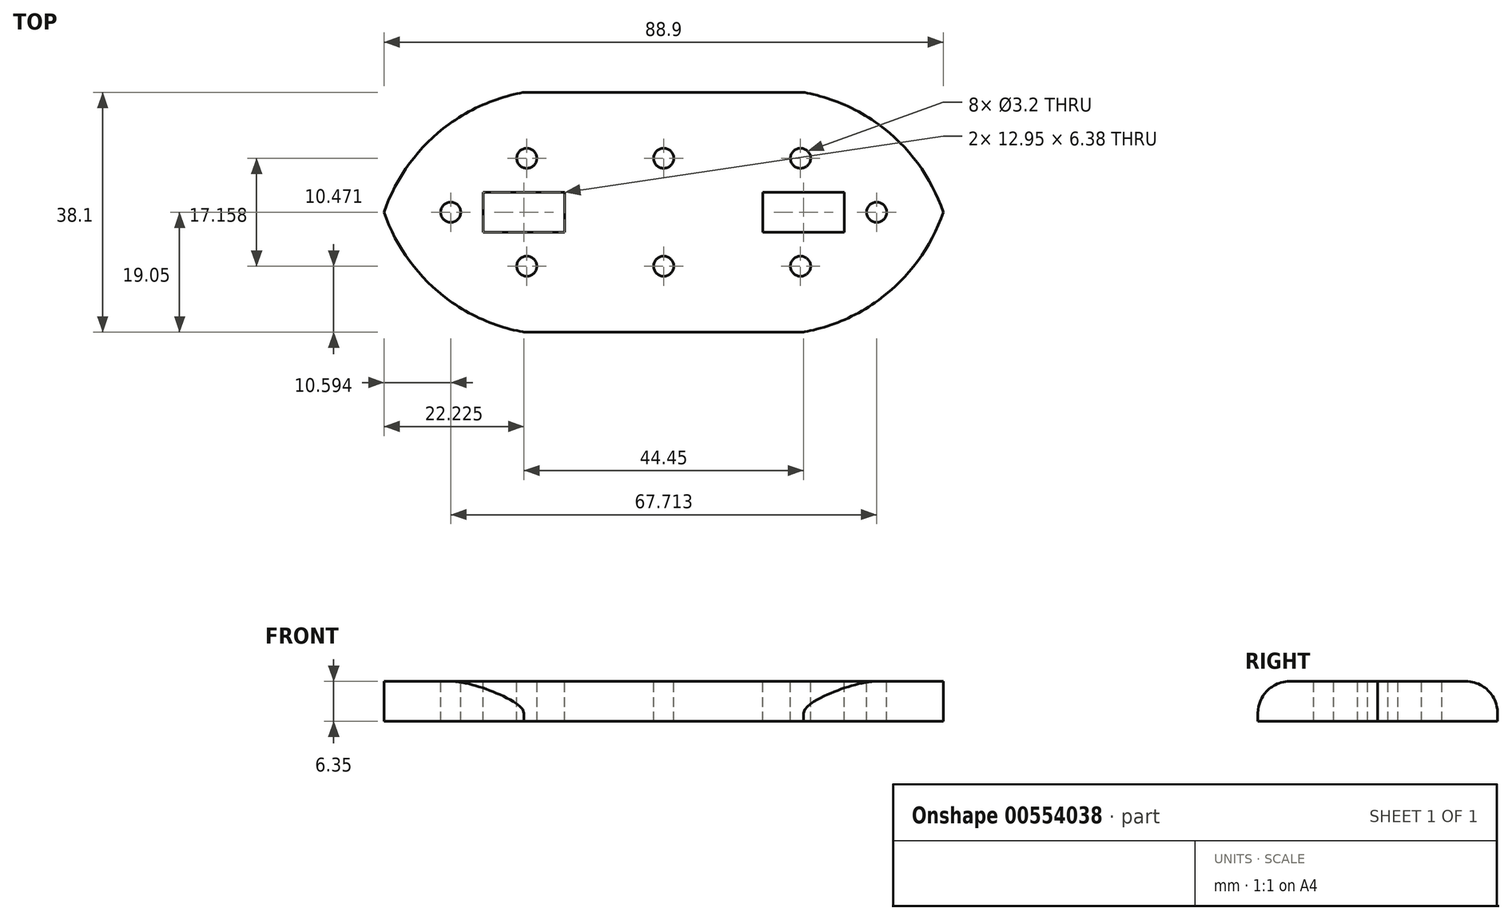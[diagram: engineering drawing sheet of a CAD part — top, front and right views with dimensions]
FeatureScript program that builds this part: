
annotation { "Feature Type Name" : "Feature", "Feature Type Description" : "" }
export const myFeature = defineFeature(function(context is Context, id is Id, definition is map)
    precondition{}
    {
        {
            var Q0;
            Q0=qCreatedBy(makeId("Top.planeOp"),FACE);
            var sketch = newSketch(context, id + "F0", { "sketchPlane" : qUnion([Q0])});
            skLineSegment(sketch, "E0.bottom", {"start": v(44.45, 19.05) * mm, "end": v(-44.45, 19.05) * mm});
            skLineSegment(sketch, "E0.top", {"start": v(44.45, -19.05) * mm, "end": v(-44.45, -19.05) * mm});
            skLineSegment(sketch, "E0.left", {"start": v(44.45, 19.05) * mm, "end": v(44.45, -19.05) * mm});
            skLineSegment(sketch, "E0.right", {"start": v(-44.45, 19.05) * mm, "end": v(-44.45, -19.05) * mm});
            skPoint(sketch, "E0.middle", {"position": v(0, 0) * mm});
            skSolve(sketch);
        }
        {
            var Q0;
            Q0 = qSketchRegion(id + "F0", true);
            extrude(context, id + "F1", {"entities" : qUnion([Q0]), "depth" : 6.35 * mm, "offsetDistance" : 25.4 * mm});
        }
        {
            var Q0;
            Q0=makeQuery(id+"F1.opExtrude","CAP_FACE",FACE,{"disambiguationData":[OSD([sQuery(id+"F0.wireOp",EDGE,"E0.bottom"),sQuery(id+"F0.wireOp",EDGE,"E0.top"),sQuery(id+"F0.wireOp",EDGE,"E0.left"),sQuery(id+"F0.wireOp",EDGE,"E0.right")])],"isStart":false});
            var sketch = newSketch(context, id + "F2", { "sketchPlane" : qUnion([Q0])});
            skLineSegment(sketch, "E1", {"start": v(0, 19.05) * mm, "end": v(44.45, 19.05) * mm, "construction": true});
            skLineSegment(sketch, "E2", {"start": v(-44.45, 19.05) * mm, "end": v(0, 19.05) * mm, "construction": true});
            skLineSegment(sketch, "E3", {"start": v(0, 19.05) * mm, "end": v(0, -5.07) * mm, "construction": true});
            skArc(sketch, "E4", {"start": v(-22.23, 19.05) * mm, "mid": v(-35.93, 12.55) * mm, "end": v(-44.45, 0) * mm});
            skArc(sketch, "E5.MirrorCS", {"start": v(22.23, 19.05) * mm, "mid": v(35.93, 12.55) * mm, "end": v(44.45, 0) * mm});
            skLineSegment(sketch, "E6", {"start": v(0, 0) * mm, "end": v(25.9, 0) * mm, "construction": true});
            skArc(sketch, "E7.MirrorCS", {"start": v(22.23, -19.05) * mm, "mid": v(35.93, -12.55) * mm, "end": v(44.45, 0) * mm});
            skArc(sketch, "E8.MirrorCS", {"start": v(-22.23, -19.05) * mm, "mid": v(-35.93, -12.55) * mm, "end": v(-44.45, 0) * mm});
            skLineSegment(sketch, "E9", {"start": v(-22.23, -19.05) * mm, "end": v(-55.77, -34.2) * mm, "construction": true});
            skLineSegment(sketch, "E10", {"start": v(-55.77, -34.2) * mm, "end": v(-22.23, -19.05) * mm});
            skLineSegment(sketch, "E11", {"start": v(-55.77, -34.2) * mm, "end": v(-59.27, 33.28) * mm});
            skLineSegment(sketch, "E12", {"start": v(-59.27, 33.28) * mm, "end": v(-22.22, 19.05) * mm});
            skLineSegment(sketch, "E13", {"start": v(22.23, 19.05) * mm, "end": v(83.05, 33.83) * mm});
            skLineSegment(sketch, "E14", {"start": v(83.05, 33.83) * mm, "end": v(77.7, -26.82) * mm});
            skLineSegment(sketch, "E15", {"start": v(77.7, -26.82) * mm, "end": v(22.23, -19.05) * mm});
            skSolve(sketch);
        }
        {
            var Q0;
            Q0 = qSketchRegion(id + "F2", true);
            extrude(context, id + "F3", {"entities" : qUnion([Q0]), "operationType" : NewBodyOperationType.REMOVE, "oppositeDirection" : true, "depth" : 25.4 * mm, "offsetDistance" : 25.4 * mm});
        }
        {
            var Q0;
            Q0=makeQuery(id+"F1.opExtrude","CAP_FACE",FACE,{"disambiguationData":[OSD([sQuery(id+"F0.wireOp",EDGE,"E0.bottom"),sQuery(id+"F0.wireOp",EDGE,"E0.top"),sQuery(id+"F0.wireOp",EDGE,"E0.left"),sQuery(id+"F0.wireOp",EDGE,"E0.right")])],"isStart":false});
            var sketch = newSketch(context, id + "F4", { "sketchPlane" : qUnion([Q0])});
            skLineSegment(sketch, "E16", {"start": v(0, 19.05) * mm, "end": v(0, -19.05) * mm, "construction": true});
            skLineSegment(sketch, "E17", {"start": v(-22.23, 19.05) * mm, "end": v(-22.22, -19.05) * mm, "construction": true});
            skLineSegment(sketch, "E18", {"start": v(22.22, 19.05) * mm, "end": v(22.22, -19.05) * mm, "construction": true});
            skLineSegment(sketch, "E19.bottom", {"start": v(-15.75, 3.19) * mm, "end": v(-28.7, 3.19) * mm});
            skLineSegment(sketch, "E19.top", {"start": v(-15.75, -3.19) * mm, "end": v(-28.7, -3.19) * mm});
            skLineSegment(sketch, "E19.left", {"start": v(-15.75, 3.19) * mm, "end": v(-15.75, -3.19) * mm});
            skLineSegment(sketch, "E19.right", {"start": v(-28.7, 3.19) * mm, "end": v(-28.7, -3.19) * mm});
            skPoint(sketch, "E19.middle", {"position": v(-22.22, 0) * mm});
            skLineSegment(sketch, "E20.MirrorCS", {"start": v(15.75, 3.19) * mm, "end": v(28.7, 3.19) * mm});
            skLineSegment(sketch, "E21.MirrorCS", {"start": v(15.75, -3.19) * mm, "end": v(28.7, -3.19) * mm});
            skLineSegment(sketch, "E22.MirrorCS", {"start": v(15.75, 3.19) * mm, "end": v(15.75, -3.19) * mm});
            skLineSegment(sketch, "E23.MirrorCS", {"start": v(28.7, 3.19) * mm, "end": v(28.7, -3.19) * mm});
            skSolve(sketch);
        }
        {
            var Q0;
            Q0 = qSketchRegion(id + "F4", true);
            extrude(context, id + "F5", {"entities" : qUnion([Q0]), "operationType" : NewBodyOperationType.REMOVE, "oppositeDirection" : true, "depth" : 25.4 * mm, "offsetDistance" : 25.4 * mm});
        }
        {
            var Q0;
            Q0=makeQuery(id+"F3.boolean.opBoolean","COPY",EDGE,{"derivedFrom":makeQuery(id+"F3.opExtrude","CAP_EDGE",EDGE,{"disambiguationData":[OSD([sQuery(id+"F2.wireOp",EDGE,"E8.MirrorCS")])],"isStart":true})});
            var Q1;
            Q1=makeQuery(id+"F3.boolean.opBoolean","COPY",EDGE,{"derivedFrom":makeQuery(id+"F3.opExtrude","CAP_EDGE",EDGE,{"disambiguationData":[OSD([sQuery(id+"F2.wireOp",EDGE,"E4")])],"isStart":true})});
            var Q2;
            Q2=makeQuery(id+"F1.opExtrude","CAP_EDGE",EDGE,{"disambiguationData":[OSD([sQuery(id+"F0.wireOp",EDGE,"E0.bottom")])],"isStart":false});
            var Q3;
            Q3=makeQuery(id+"F1.opExtrude","CAP_EDGE",EDGE,{"disambiguationData":[OSD([sQuery(id+"F0.wireOp",EDGE,"E0.top")])],"isStart":false});
            var Q4;
            Q4=makeQuery(id+"F3.boolean.opBoolean","COPY",EDGE,{"derivedFrom":makeQuery(id+"F3.opExtrude","CAP_EDGE",EDGE,{"disambiguationData":[OSD([sQuery(id+"F2.wireOp",EDGE,"E7.MirrorCS")])],"isStart":true})});
            var Q5;
            Q5=makeQuery(id+"F3.boolean.opBoolean","COPY",EDGE,{"derivedFrom":makeQuery(id+"F3.opExtrude","CAP_EDGE",EDGE,{"disambiguationData":[OSD([sQuery(id+"F2.wireOp",EDGE,"E5.MirrorCS")])],"isStart":true})});
            fillet(context, id + "F6", {"entities" : qUnion([Q0, Q1, Q2, Q3, Q4, Q5]), "tangentPropagation" : true, "radius" : 5.08 * mm, "defaultsChanged" : false, "vertexSettings" : [], "allowEdgeOverflow" : false});
        }
        {
            var Q0;
            Q0=makeQuery(id+"F1.opExtrude","CAP_FACE",FACE,{"disambiguationData":[OSD([sQuery(id+"F0.wireOp",EDGE,"E0.bottom"),sQuery(id+"F0.wireOp",EDGE,"E0.top"),sQuery(id+"F0.wireOp",EDGE,"E0.left"),sQuery(id+"F0.wireOp",EDGE,"E0.right")])],"isStart":false});
            var sketch = newSketch(context, id + "F7", { "sketchPlane" : qUnion([Q0])});
            skLineSegment(sketch, "E24", {"start": v(-21.75, 13.97) * mm, "end": v(-21.75, -13.97) * mm, "construction": true});
            skLineSegment(sketch, "E25", {"start": v(-39.01, 0) * mm, "end": v(39.01, 0) * mm, "construction": true});
            skLineSegment(sketch, "E26", {"start": v(0, 13.97) * mm, "end": v(0, -13.97) * mm, "construction": true});
            skLineSegment(sketch, "E27", {"start": v(21.75, 13.97) * mm, "end": v(21.75, -13.97) * mm, "construction": true});
            skLineSegment(sketch, "E28", {"start": v(-39.01, 0) * mm, "end": v(-28.7, 0) * mm, "construction": true});
            skLineSegment(sketch, "E29", {"start": v(28.7, 0) * mm, "end": v(39.01, 0) * mm, "construction": true});
            skLineSegment(sketch, "E30", {"start": v(-21.75, 13.97) * mm, "end": v(-21.75, 3.19) * mm, "construction": true});
            skLineSegment(sketch, "E31", {"start": v(-21.75, -13.97) * mm, "end": v(-21.75, -3.19) * mm, "construction": true});
            skLineSegment(sketch, "E32", {"start": v(21.75, -3.19) * mm, "end": v(21.75, -13.97) * mm, "construction": true});
            skLineSegment(sketch, "E33", {"start": v(21.75, 3.19) * mm, "end": v(21.75, 13.97) * mm, "construction": true});
            skCircle(sketch, "E34", {"center": v(-33.86, 0) * mm, "radius": 1.6 * mm});
            skCircle(sketch, "E35", {"center": v(-21.75, 8.58) * mm, "radius": 1.6 * mm});
            skCircle(sketch, "E36.MirrorC", {"center": v(33.86, 0) * mm, "radius": 1.6 * mm});
            skCircle(sketch, "E37.MirrorC", {"center": v(21.75, 8.58) * mm, "radius": 1.6 * mm});
            skLineSegment(sketch, "E38.MirrorCS", {"start": v(39.01, 0) * mm, "end": v(-39.01, 0) * mm, "construction": true});
            skCircle(sketch, "E39.MirrorC", {"center": v(-21.75, -8.58) * mm, "radius": 1.6 * mm});
            skCircle(sketch, "E40.MirrorC", {"center": v(21.75, -8.58) * mm, "radius": 1.6 * mm});
            skLineSegment(sketch, "E41", {"start": v(-21.75, 0) * mm, "end": v(0, 0) * mm, "construction": true});
            skLineSegment(sketch, "E42", {"start": v(0, 0) * mm, "end": v(-10.88, 0) * mm, "construction": true});
            skLineSegment(sketch, "E43", {"start": v(-10.88, 0) * mm, "end": v(-10.88, 11.47) * mm, "construction": true});
            skCircle(sketch, "E44.MirrorC", {"center": v(0, 8.58) * mm, "radius": 1.6 * mm});
            skCircle(sketch, "E45.MirrorC", {"center": v(0, -8.58) * mm, "radius": 1.6 * mm});
            skSolve(sketch);
        }
        {
            var Q0;
            Q0 = qSketchRegion(id + "F7", true);
            extrude(context, id + "F8", {"entities" : qUnion([Q0]), "operationType" : NewBodyOperationType.REMOVE, "oppositeDirection" : true, "depth" : 25.4 * mm, "offsetDistance" : 25.4 * mm});
        }
    });
